# Revit family: RN 81040 Optipress-Aquaplus-Raccordo
name_source: partatom
category: Rohrformteile
units: mm (PartAtom-declared; Revit-internal decimal feet)

## family parameters
Arbeitsebenenbasiert = Nein
Beim Laden mit Abzugskörper schneiden = Nein
Bemaßung runder Anschluss = Durchmesser verwenden
Gemeinsam genutzt = Nein
Immer vertikal = Ja
Teiletyp = Verbindung

## types (3) — shared parameters
1.010.00.2 Number of the part of the guideline = 29
1.010.00.3 Issue date (month) of the guideline = 201308
1.010.00.4 Manufacturer name = R. Nussbaum AG
1.010.00.5 Revision date of the file = 20190521
1.100.00.4 Product designation = Fornitura
1.110.00.2 Index = 4
1.110.00.4 Product designation = Optipress
1.960/3L.00.8 Link (URL) = https://www.nussbaum.ch
29.700.00.4 Product name = Optipress-Aquaplus-Raccordo, serrabile con rubinetto a sfera
29.700.00.5 Product identification = 2
29.700.00.6 Cross-sectional shape = 1
29.700.00.7 Nominal size system = DN
29.700.00.8 Nominal pressure system = PN
29.710.02.4 Nominal pressure = 10
29.710.02.5 max. allowed overpressure [hPa] = 1000
29.710.02.7 max. allowed continuous operating pressure [hPa] = 1000
29.710.02.9 max. allowed continuous operating temperature [°C] = 90
Connector Visibility = Nein
EnclosingSpace Visibility = Nein

## per-type parameters (varying)
| type | 1.800.00.3 BS number | 1.810.00.3 Manufacturer’s reference number | 1.810.00.4 DATANORM number | 1.810.00.5 StLB number | 1.810.00.6 GTIN number | 29.710.02.10 Fitting weight [kg] | 29.710.02.3 Designation | CONNECTOR0_DIAMETER_dX_0r | CONNECTOR0_dX_01 | CONNECTOR0_ref_dX | CONNECTOR1_DIAMETER_dX_0r | CONNECTOR1_dX_00 | CONNECTOR1_dX_01 | CONNECTOR1_ref_dX | R. Nussbaum AG 81040.22 it Visibility | R. Nussbaum AG 81040.23 it Visibility | R. Nussbaum AG 81040.24 it Visibility |
| 81040.22, Optipress-Aquaplus-Raccordo, serrabile con rubinetto a sfera, DN=12, L=76 | 01900400000000000000000000000000000000000000000041000000000000000001 | 81040.22 | 81040.22 | 671.472 | 7612945654724 | 0.245 | Optipress-Aquaplus-Raccordo, serrabile con rubinetto a sfera, DN=12, L=76 | 12 mm  [stored 0.0393701 ft] | 22 mm | 22 mm | 20 mm | 70 mm | 85 mm | 70 mm | Ja | Nein | Nein |
| 81040.23, Optipress-Aquaplus-Raccordo, serrabile con rubinetto a sfera, DN=15, L=76 | 01900400000000000000000000000000000000000000000041000000000000000002 | 81040.23 | 81040.23 | 671.473 | 7612945654731 | 0.249 | Optipress-Aquaplus-Raccordo, serrabile con rubinetto a sfera, DN=15, L=76 | 15 mm  [stored 0.0492126 ft] | 22 mm | 22 mm | 20 mm | 69 mm | 84 mm | 69 mm | Nein | Ja | Nein |
| 81040.24, Optipress-Aquaplus-Raccordo, serrabile con rubinetto a sfera, DN=20, L=81 | 01900400000000000000000000000000000000000000000041000000000000000003 | 81040.24 | 81040.24 | 671.474 | 7612945654748 | 0.307 | Optipress-Aquaplus-Raccordo, serrabile con rubinetto a sfera, DN=20, L=81 | 20 mm | 24 mm  [stored 0.0787402 ft] | 24 mm  [stored 0.0787402 ft] | 25 mm  [stored 0.082021 ft] | 72 mm | 89 mm | 72 mm | Nein | Nein | Ja |

note: column(s) folded — value = type name in every type: 1.800.00.4 Comment field

note: [stored X ft] marks values corroborated as IEEE doubles in the binary element streams (Revit-internal decimal feet)

## geometry (parser evidence)
native form markers: Sweep x3
no freeform markers — native parametric forms only
